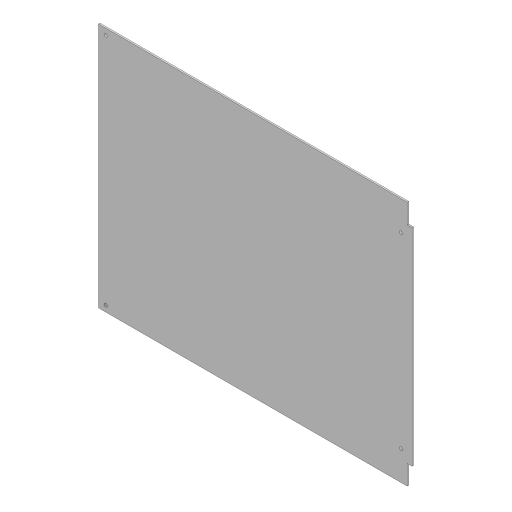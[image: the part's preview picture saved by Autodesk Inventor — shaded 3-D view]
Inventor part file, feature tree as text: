
AUTODESK INVENTOR PART (.ipt)
format: ipt  version: 2023 (Build 270158000, 158)  size: 111,104 bytes
history: native  units: mm
features: extrude x2, sketch x1, hole x1
ambient origin geometry x8: Origin, YZ Plane, XZ Plane, XY Plane, X Axis, Y Axis, Z Axis, Center Point
bodies: Solid1 (feature_tree)
feature tree (4):
  sketch  "Sketch1"  dims[d2=638.0mm d3=500.0mm d10=22.5mm d11=15.5mm d12=12.5mm d13=12.5mm d14=60.0mm d15=60.0mm d16=3.0mm d17=0.0mm d18=6.4mm d19=6.0mm d20=4.0mm d21=2.0mm d22=90.0deg d23=8.0mm d24=20.594885mm d29=10.0mm d30=0.0mm d31=0.0mm]
  extrude  "Extrusion1"  Depth=500.0mm
  hole  "Hole1"  [1 undecoded]
  extrude  "Extrusion3"  Depth=10.0mm
note: 1 required parameter value undecoded (feature->parameter linkage not recoverable at this tier; creation-order binding heuristic only, values carry confidence <= 0.55)
